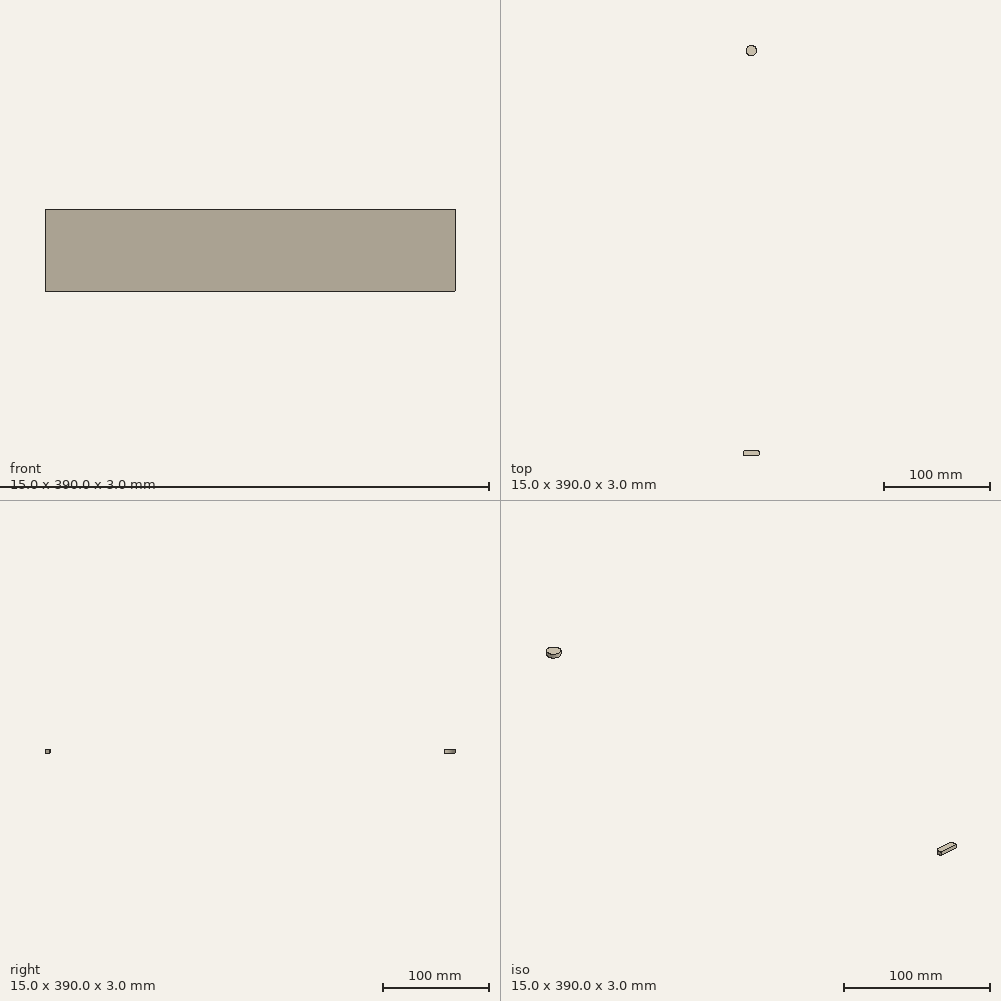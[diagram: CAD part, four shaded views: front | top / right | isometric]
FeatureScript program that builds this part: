
annotation { "Feature Type Name" : "Feature", "Feature Type Description" : "" }
export const myFeature = defineFeature(function(context is Context, id is Id, definition is map)
    precondition{}
    {
        {
            var Q0;
            Q0=qCreatedBy(makeId("Top.planeOp"),FACE);
            var sketch = newSketch(context, id + "F0", { "sketchPlane" : qUnion([Q0])});
            skLineSegment(sketch, "E0.bottom", {"start": v(240, -240) * mm, "end": v(-240, -240) * mm});
            skLineSegment(sketch, "E0.top", {"start": v(240, 240) * mm, "end": v(-240, 240) * mm});
            skLineSegment(sketch, "E0.left", {"start": v(240, -240) * mm, "end": v(240, 240) * mm});
            skLineSegment(sketch, "E0.right", {"start": v(-240, -240) * mm, "end": v(-240, 240) * mm});
            skPoint(sketch, "E0.middle", {"position": v(0, 0) * mm});
            skSolve(sketch);
        }
        {
            var Q0;
            Q0=makeQuery(id+"F0.imprint","IMPRINT",FACE,{"disambiguationData":[TD([[makeQuery(id+"F0.imprint","IMPRINT",EDGE,{"derivedFrom":sQuery(id+"F0.wireOp",EDGE,"E0.bottom")}),-1.0]])]});
            extrude(context, id + "F1", {"entities" : qUnion([Q0]), "depth" : 3 * mm, "offsetDistance" : 25 * mm});
        }
        {
            var Q0;
            Q0=makeQuery(id+"F1.opExtrude","CAP_FACE",FACE,{"disambiguationData":[OSD([sQuery(id+"F0.wireOp",EDGE,"E0.bottom"),sQuery(id+"F0.wireOp",EDGE,"E0.top"),sQuery(id+"F0.wireOp",EDGE,"E0.left"),sQuery(id+"F0.wireOp",EDGE,"E0.right")])],"isStart":false});
            var sketch = newSketch(context, id + "F2", { "sketchPlane" : qUnion([Q0])});
            skLineSegment(sketch, "E1.bottom", {"start": v(-240, 240) * mm, "end": v(-200, 240) * mm});
            skLineSegment(sketch, "E1.top", {"start": v(-240, 200) * mm, "end": v(-200, 200) * mm});
            skLineSegment(sketch, "E1.left", {"start": v(-240, 240) * mm, "end": v(-240, 200) * mm});
            skLineSegment(sketch, "E1.right", {"start": v(-200, 240) * mm, "end": v(-200, 200) * mm});
            skLineSegment(sketch, "E2.bottom", {"start": v(240, 240) * mm, "end": v(200, 240) * mm});
            skLineSegment(sketch, "E2.top", {"start": v(240, 200) * mm, "end": v(200, 200) * mm});
            skLineSegment(sketch, "E2.left", {"start": v(240, 240) * mm, "end": v(240, 200) * mm});
            skLineSegment(sketch, "E2.right", {"start": v(200, 240) * mm, "end": v(200, 200) * mm});
            skLineSegment(sketch, "E3.bottom", {"start": v(240, -240) * mm, "end": v(200, -240) * mm});
            skLineSegment(sketch, "E3.top", {"start": v(240, -200) * mm, "end": v(200, -200) * mm});
            skLineSegment(sketch, "E3.left", {"start": v(240, -240) * mm, "end": v(240, -200) * mm});
            skLineSegment(sketch, "E3.right", {"start": v(200, -240) * mm, "end": v(200, -200) * mm});
            skLineSegment(sketch, "E4.bottom", {"start": v(-240, -240) * mm, "end": v(-200, -240) * mm});
            skLineSegment(sketch, "E4.top", {"start": v(-240, -200) * mm, "end": v(-200, -200) * mm});
            skLineSegment(sketch, "E4.left", {"start": v(-240, -240) * mm, "end": v(-240, -200) * mm});
            skLineSegment(sketch, "E4.right", {"start": v(-200, -240) * mm, "end": v(-200, -200) * mm});
            skSolve(sketch);
        }
        {
            var Q0;
            Q0 = qSketchRegion(id + "F2", true);
            extrude(context, id + "F3", {"entities" : qUnion([Q0]), "operationType" : NewBodyOperationType.REMOVE, "oppositeDirection" : true, "depth" : 25 * mm, "offsetDistance" : 25 * mm});
        }
        {
            var Q0;
            Q0=makeQuery(id+"F1.opExtrude","CAP_FACE",FACE,{"disambiguationData":[OSD([sQuery(id+"F0.wireOp",EDGE,"E0.bottom"),sQuery(id+"F0.wireOp",EDGE,"E0.top"),sQuery(id+"F0.wireOp",EDGE,"E0.left"),sQuery(id+"F0.wireOp",EDGE,"E0.right")])],"isStart":false});
            var sketch = newSketch(context, id + "F4", { "sketchPlane" : qUnion([Q0])});
            skLineSegment(sketch, "E5.bottom", {"start": v(-190, -190) * mm, "end": v(190, -190) * mm});
            skLineSegment(sketch, "E5.top", {"start": v(-190, 190) * mm, "end": v(190, 190) * mm});
            skLineSegment(sketch, "E5.left", {"start": v(-190, -190) * mm, "end": v(-190, 190) * mm});
            skLineSegment(sketch, "E5.right", {"start": v(190, -190) * mm, "end": v(190, 190) * mm});
            skPoint(sketch, "E6", {"position": v(0, 190) * mm});
            skPoint(sketch, "E7", {"position": v(-190, -190) * mm});
            skPoint(sketch, "E8", {"position": v(190, -190) * mm});
            skCircle(sketch, "E9", {"center": v(0, 190) * mm, "radius": 5 * mm});
            skCircle(sketch, "E10", {"center": v(-190, -190) * mm, "radius": 5 * mm});
            skCircle(sketch, "E11", {"center": v(190, -190) * mm, "radius": 5 * mm});
            skPoint(sketch, "E12", {"position": v(0, -190) * mm});
            skLineSegment(sketch, "E13.bottom", {"start": v(7.5, -190) * mm, "end": v(-7.5, -190) * mm});
            skLineSegment(sketch, "E13.top", {"start": v(7.5, -190) * mm, "end": v(-7.5, -190) * mm});
            skLineSegment(sketch, "E13.left", {"start": v(7.5, -190) * mm, "end": v(7.5, -190) * mm});
            skLineSegment(sketch, "E13.right", {"start": v(-7.5, -190) * mm, "end": v(-7.5, -190) * mm});
            skPoint(sketch, "E14", {"position": v(-7.5, -190) * mm});
            skPoint(sketch, "E15", {"position": v(7.5, -190) * mm});
            skLineSegment(sketch, "E16.bottom", {"start": v(-7.5, -190) * mm, "end": v(7.5, -190) * mm});
            skLineSegment(sketch, "E16.top", {"start": v(-7.5, -195) * mm, "end": v(7.5, -195) * mm});
            skLineSegment(sketch, "E16.left", {"start": v(-7.5, -190) * mm, "end": v(-7.5, -195) * mm});
            skLineSegment(sketch, "E16.right", {"start": v(7.5, -190) * mm, "end": v(7.5, -195) * mm});
            skSolve(sketch);
        }
        {
            var Q0;
            {var subQ0=sQuery(id+"F4.wireOp",EDGE,"E9");var subQ1=sQuery(id+"F4.wireOp",EDGE,"E5.top");var subQ2=makeQuery(id+"F4.imprint","INTERSECT",VERTEX,{"disambiguationData":[OD(0.0)],"derivedFrom":[subQ1,subQ0]});Q0=makeQuery(id+"F4.imprint","IMPRINT",FACE,{"disambiguationData":[TD([[makeQuery(id+"F4.imprint","IMPRINT",EDGE,{"disambiguationData":[TD([[subQ2,-1.0]])],"derivedFrom":subQ1}),-1.0]])]});}
            var Q1;
            {var subQ0=sQuery(id+"F4.wireOp",EDGE,"E9");var subQ1=sQuery(id+"F4.wireOp",EDGE,"E5.top");var subQ2=makeQuery(id+"F4.imprint","INTERSECT",VERTEX,{"disambiguationData":[OD(0.0)],"derivedFrom":[subQ1,subQ0]});Q1=makeQuery(id+"F4.imprint","IMPRINT",FACE,{"disambiguationData":[TD([[makeQuery(id+"F4.imprint","IMPRINT",EDGE,{"disambiguationData":[TD([[subQ2,-1.0]])],"derivedFrom":subQ1}),1.0]])]});}
            var Q2;
            {var subQ0=sQuery(id+"F4.wireOp",EDGE,"E5.left");var subQ1=sQuery(id+"F4.wireOp",EDGE,"E5.bottom");var subQ2=makeQuery(id+"F4.imprint","INTERSECT",VERTEX,{"derivedFrom":[subQ1,subQ0]});Q2=makeQuery(id+"F4.imprint","IMPRINT",FACE,{"disambiguationData":[TD([[makeQuery(id+"F4.imprint","IMPRINT",EDGE,{"disambiguationData":[TD([[subQ2,-1.0]])],"derivedFrom":subQ1}),-1.0]])]});}
            var Q3;
            {var subQ0=sQuery(id+"F4.wireOp",EDGE,"E5.left");var subQ1=sQuery(id+"F4.wireOp",EDGE,"E5.bottom");var subQ2=makeQuery(id+"F4.imprint","INTERSECT",VERTEX,{"derivedFrom":[subQ1,subQ0]});Q3=makeQuery(id+"F4.imprint","IMPRINT",FACE,{"disambiguationData":[TD([[makeQuery(id+"F4.imprint","IMPRINT",EDGE,{"disambiguationData":[TD([[subQ2,-1.0]])],"derivedFrom":subQ1}),1.0]])]});}
            var Q4;
            {var subQ0=sQuery(id+"F4.wireOp",EDGE,"E5.right");var subQ1=sQuery(id+"F4.wireOp",EDGE,"E5.bottom");var subQ2=makeQuery(id+"F4.imprint","INTERSECT",VERTEX,{"derivedFrom":[subQ1,subQ0]});Q4=makeQuery(id+"F4.imprint","IMPRINT",FACE,{"disambiguationData":[TD([[makeQuery(id+"F4.imprint","IMPRINT",EDGE,{"disambiguationData":[TD([[subQ2,1.0]])],"derivedFrom":subQ1}),1.0]])]});}
            var Q5;
            {var subQ0=sQuery(id+"F4.wireOp",EDGE,"E5.right");var subQ1=sQuery(id+"F4.wireOp",EDGE,"E5.bottom");var subQ2=makeQuery(id+"F4.imprint","INTERSECT",VERTEX,{"derivedFrom":[subQ1,subQ0]});Q5=makeQuery(id+"F4.imprint","IMPRINT",FACE,{"disambiguationData":[TD([[makeQuery(id+"F4.imprint","IMPRINT",EDGE,{"disambiguationData":[TD([[subQ2,1.0]])],"derivedFrom":subQ1}),-1.0]])]});}
            extrude(context, id + "F5", {"entities" : qUnion([Q0, Q1, Q2, Q3, Q4, Q5]), "operationType" : NewBodyOperationType.REMOVE, "oppositeDirection" : true, "depth" : 25 * mm, "offsetDistance" : 25 * mm});
        }
        {
            var Q0;
            Q0=sQuery(id+"F4.wireOp",VERTEX,"E14");
            var Q1;
            Q1=sQuery(id+"F4.wireOp",VERTEX,"E15");
            var Q2;
            Q2=makeQuery(id+"F1.opExtrude","SWEPT_BODY",BODY,{"disambiguationData":[OSD([sQuery(id+"F0.wireOp",EDGE,"E0.bottom"),sQuery(id+"F0.wireOp",EDGE,"E0.top"),sQuery(id+"F0.wireOp",EDGE,"E0.left"),sQuery(id+"F0.wireOp",EDGE,"E0.right")])]});
            hole(context, id + "F6", {"style" : HoleStyle.SIMPLE, "endStyle" : HoleEndStyle.THROUGH, "holeDiameter" : 3 * mm, "majorDiameter" : 5 * mm, "isTappedThrough" : true, "tappedDepth" : 12 * mm, "tapClearance" : 3, "locations" : qUnion([Q0, Q1]), "scope" : qUnion([Q2])});
        }
    });
